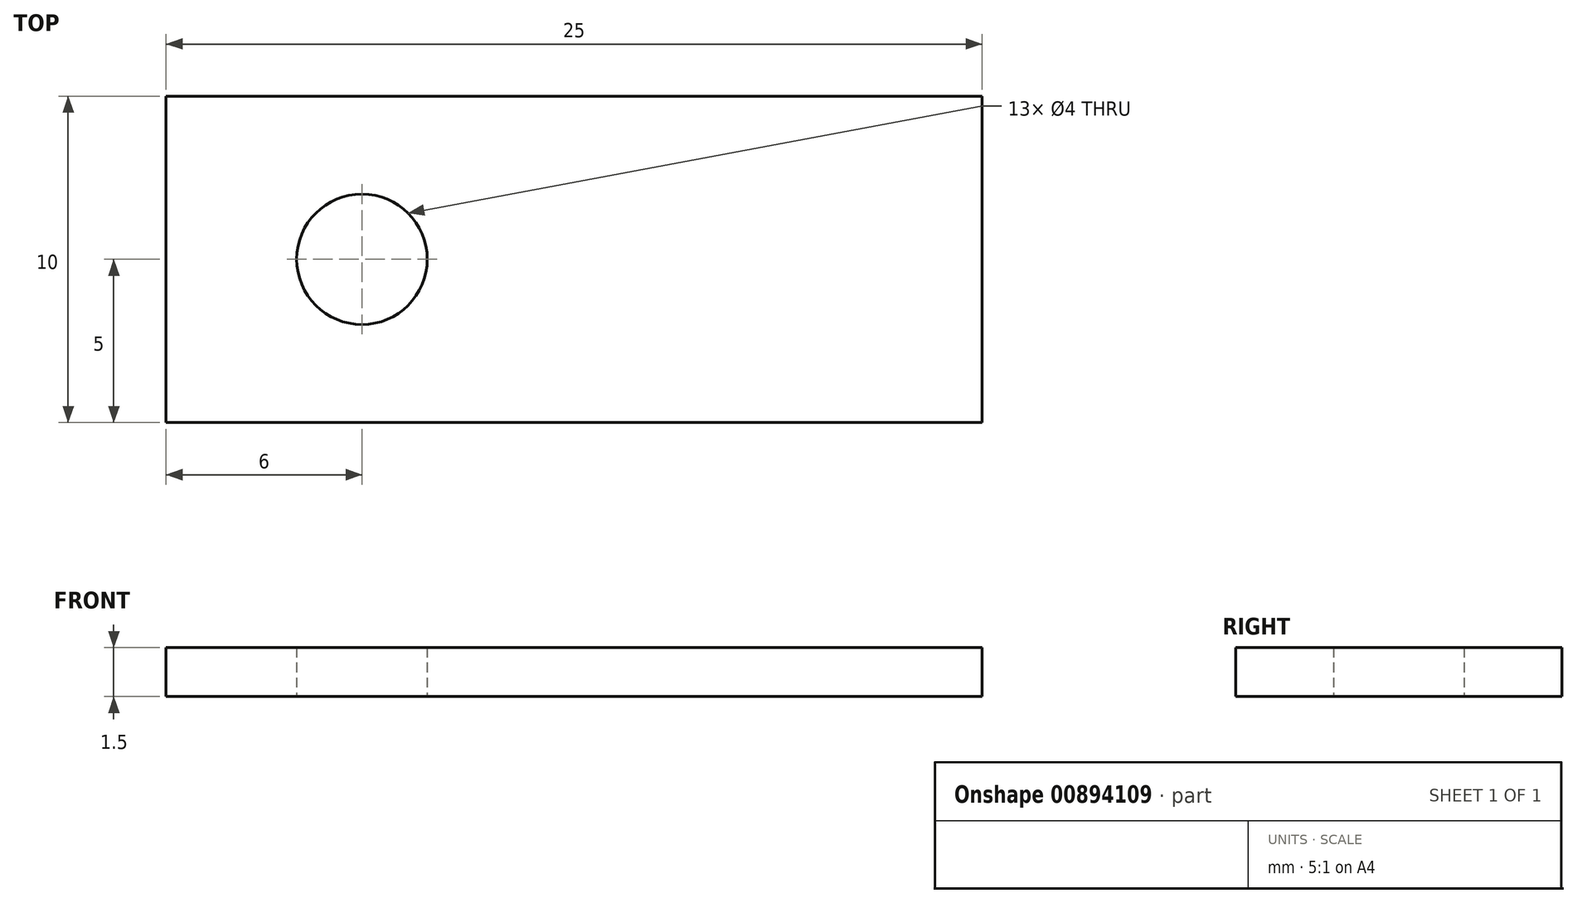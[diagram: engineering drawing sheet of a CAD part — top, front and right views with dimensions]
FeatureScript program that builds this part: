
annotation { "Feature Type Name" : "Feature", "Feature Type Description" : "" }
export const myFeature = defineFeature(function(context is Context, id is Id, definition is map)
    precondition{}
    {
        {
            var Q0;
            Q0=qCreatedBy(makeId("Top.planeOp"),FACE);
            var sketch = newSketch(context, id + "F0", { "sketchPlane" : qUnion([Q0])});
            skLineSegment(sketch, "E0.bottom", {"start": v(12.5, -5) * mm, "end": v(-12.5, -5) * mm});
            skLineSegment(sketch, "E0.top", {"start": v(12.5, 5) * mm, "end": v(-12.5, 5) * mm});
            skLineSegment(sketch, "E0.left", {"start": v(12.5, -5) * mm, "end": v(12.5, 5) * mm});
            skLineSegment(sketch, "E0.right", {"start": v(-12.5, -5) * mm, "end": v(-12.5, 5) * mm});
            skPoint(sketch, "E0.middle", {"position": v(0, 0) * mm});
            skCircle(sketch, "E1", {"center": v(-6.5, 0) * mm, "radius": 2 * mm});
            skSolve(sketch);
        }
        {
            var Q0;
            Q0=makeQuery(id+"F0.imprint","IMPRINT",FACE,{"disambiguationData":[TD([[makeQuery(id+"F0.imprint","IMPRINT",EDGE,{"derivedFrom":sQuery(id+"F0.wireOp",EDGE,"E0.bottom")}),-1.0]])]});
            extrude(context, id + "F1", {"entities" : qUnion([Q0]), "depth" : 1.5 * mm, "offsetDistance" : 25 * mm});
        }
    });
